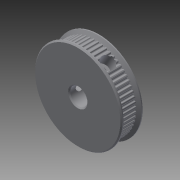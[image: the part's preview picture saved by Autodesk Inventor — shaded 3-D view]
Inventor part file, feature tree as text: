
AUTODESK INVENTOR PART (.ipt)
format: ipt  version: 2020 (Build 240168000, 168)  size: 680,960 bytes
history: native  units: mm
features: sketch x4, extrude x3, revolve x2, pattern_circular x2, plane x2, chamfer x2, fillet x1
ambient origin geometry x8: Origin, YZ Plane, XZ Plane, XY Plane, X Axis, Y Axis, Z Axis, Center Point
bodies: Solid1 (feature_tree)
feature tree (16):
  revolve  "Revolution1"  [1 undecoded]
  extrude  "Extrusion1"  Depth=10.0mm TaperAngle=360.0deg
  fillet  "Fillet1"  Radius=18.85mm
  pattern_circular  "Circular Pattern1"  [2 undecoded]
  sketch  "Sketch3"  dims[d10=10.0mm d11=0.0mm d12=600.0mm d13=360.0deg d18=18.85mm]
  revolve  "Revolution2"  [1 undecoded]
  plane  "Work Plane1"
  extrude  "Extrusion2"  Depth=4.0mm
  chamfer  "Chamfer1"  Angle=120.0deg  [1 undecoded]
  plane  "Work Plane2"
  extrude  "Extrusion3"  Depth=4.0mm
  pattern_circular  "Circular Pattern2"  [2 undecoded]
  chamfer  "Chamfer2"  Distance=1.7mm
  sketch  "Sketch2"  dims[d7=90.0deg d8=1.1mm]
  sketch  "Sketch4"  dims[d19=0.3mm]
  sketch  "Sketch5"  dims[d20=7.5mm d21=1.0mm d22=1.5mm d23=0.5mm d24=120.0deg d25=4.0mm d26=18.85mm d27=1.7mm d28=1.7mm d29=90.0deg d31=-7.5mm d32=5.7mm d33=5.7mm d34=2.6mm d35=0.0mm d36=5.0mm d37=0.5mm d38=2.0mm d39=45.0deg d40=20.0mm d41=120.0deg d43=0.5mm d44=2.0mm d45=45.0deg d46=1.5mm d47=2.0mm d48=135.0deg d49=-3.0mm d50=6.0mm d51=30.71mm d52=0.0mm]
note: 7 required parameter values undecoded (feature->parameter linkage not recoverable at this tier; creation-order binding heuristic only, values carry confidence <= 0.55)